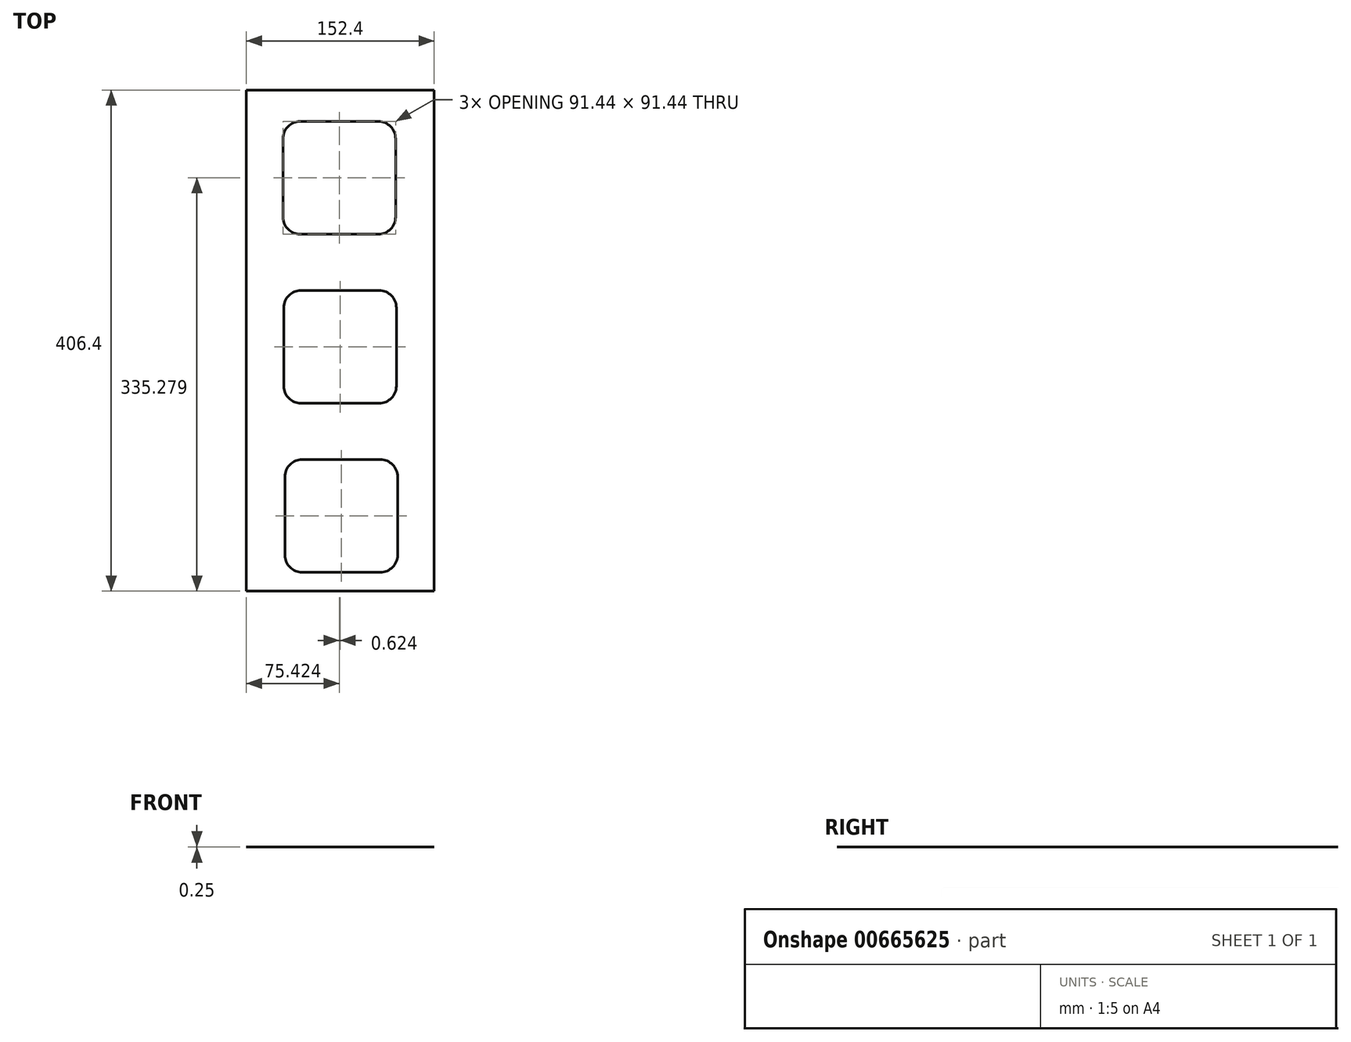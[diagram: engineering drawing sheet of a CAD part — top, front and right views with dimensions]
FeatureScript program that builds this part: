
annotation { "Feature Type Name" : "Feature", "Feature Type Description" : "" }
export const myFeature = defineFeature(function(context is Context, id is Id, definition is map)
    precondition{}
    {
        {
            var Q0;
            Q0=qCreatedBy(makeId("Top.planeOp"),FACE);
            var sketch = newSketch(context, id + "F0", { "sketchPlane" : qUnion([Q0])});
            skLineSegment(sketch, "E0.bottom", {"start": v(-76.2, 289.33) * mm, "end": v(76.2, 289.33) * mm});
            skLineSegment(sketch, "E0.top", {"start": v(-76.2, -117.07) * mm, "end": v(76.2, -117.07) * mm});
            skLineSegment(sketch, "E0.left", {"start": v(-76.2, 289.33) * mm, "end": v(-76.2, -117.07) * mm});
            skLineSegment(sketch, "E0.right", {"start": v(76.2, 289.33) * mm, "end": v(76.2, -117.07) * mm});
            skLineSegment(sketch, "E1", {"start": v(0, 187.73) * mm, "end": v(0, -142.9) * mm, "construction": true});
            skPoint(sketch, "E1.endSnap0", {"position": v(0, -117.07) * mm});
            skSolve(sketch);
        }
        {
            var Q0;
            Q0=qSketchRegion(id+"F0",true);
            extrude(context, id + "F1", {"entities" : qUnion([Q0]), "depth" : 0.25 * mm, "offsetDistance" : 25.4 * mm});
        }
        {
            var Q0;
            Q0=makeQuery(id+"F1.opExtrude","CAP_FACE",FACE,{"disambiguationData":[OSD([sQuery(id+"F0.wireOp",EDGE,"E0.bottom"),sQuery(id+"F0.wireOp",EDGE,"E0.top"),sQuery(id+"F0.wireOp",EDGE,"E0.left"),sQuery(id+"F0.wireOp",EDGE,"E0.right")])],"isStart":false});
            var sketch = newSketch(context, id + "F2", { "sketchPlane" : qUnion([Q0])});
            skLineSegment(sketch, "E2", {"start": v(0, 183.82) * mm, "end": v(0, -138.36) * mm, "construction": true});
            skLineSegment(sketch, "E3.bottom", {"start": v(-32.53, 263.93) * mm, "end": v(30.97, 263.93) * mm});
            skLineSegment(sketch, "E3.top", {"start": v(-32.53, 172.49) * mm, "end": v(30.97, 172.49) * mm});
            skLineSegment(sketch, "E3.left", {"start": v(-46.5, 249.96) * mm, "end": v(-46.5, 186.46) * mm});
            skLineSegment(sketch, "E3.right", {"start": v(44.94, 249.96) * mm, "end": v(44.94, 186.46) * mm});
            skPoint(sketch, "E4.visualSharp", {"position": v(-46.5, 263.93) * mm});
            skArc(sketch, "E4.filletArc", {"start": v(-32.53, 263.93) * mm, "mid": v(-42.4, 259.84) * mm, "end": v(-46.5, 249.96) * mm});
            skPoint(sketch, "E5.visualSharp", {"position": v(44.94, 263.93) * mm});
            skArc(sketch, "E5.filletArc", {"start": v(44.94, 249.96) * mm, "mid": v(40.85, 259.84) * mm, "end": v(30.97, 263.93) * mm});
            skPoint(sketch, "E6.visualSharp", {"position": v(44.94, 172.49) * mm});
            skArc(sketch, "E6.filletArc", {"start": v(30.97, 172.49) * mm, "mid": v(40.85, 176.58) * mm, "end": v(44.94, 186.46) * mm});
            skPoint(sketch, "E7.visualSharp", {"position": v(-46.5, 172.49) * mm});
            skArc(sketch, "E7.filletArc", {"start": v(-46.5, 186.46) * mm, "mid": v(-42.4, 176.58) * mm, "end": v(-32.53, 172.49) * mm});
            skSolve(sketch);
        }
        {
            var Q0;
            Q0=makeQuery(id+"F1.opExtrude","CAP_FACE",FACE,{"disambiguationData":[OSD([sQuery(id+"F0.wireOp",EDGE,"E0.bottom"),sQuery(id+"F0.wireOp",EDGE,"E0.top"),sQuery(id+"F0.wireOp",EDGE,"E0.left"),sQuery(id+"F0.wireOp",EDGE,"E0.right")])],"isStart":false});
            var sketch = newSketch(context, id + "F3", { "sketchPlane" : qUnion([Q0])});
            skLineSegment(sketch, "E8", {"start": v(0, 0) * mm, "end": v(0, -132.12) * mm, "construction": true});
            skLineSegment(sketch, "E9.bottom", {"start": v(-31.9, 126.77) * mm, "end": v(31.6, 126.77) * mm});
            skLineSegment(sketch, "E9.top", {"start": v(-31.9, 35.33) * mm, "end": v(31.6, 35.33) * mm});
            skLineSegment(sketch, "E9.left", {"start": v(-45.87, 112.8) * mm, "end": v(-45.87, 49.3) * mm});
            skLineSegment(sketch, "E9.right", {"start": v(45.57, 112.8) * mm, "end": v(45.57, 49.3) * mm});
            skPoint(sketch, "E10.visualSharp", {"position": v(-45.87, 126.77) * mm});
            skArc(sketch, "E10.filletArc", {"start": v(-31.9, 126.77) * mm, "mid": v(-41.78, 122.68) * mm, "end": v(-45.87, 112.8) * mm});
            skPoint(sketch, "E11.visualSharp", {"position": v(45.57, 126.77) * mm});
            skArc(sketch, "E11.filletArc", {"start": v(45.57, 112.8) * mm, "mid": v(41.48, 122.68) * mm, "end": v(31.6, 126.77) * mm});
            skPoint(sketch, "E12.visualSharp", {"position": v(45.57, 35.33) * mm});
            skArc(sketch, "E12.filletArc", {"start": v(31.6, 35.33) * mm, "mid": v(41.48, 39.42) * mm, "end": v(45.57, 49.3) * mm});
            skPoint(sketch, "E13.visualSharp", {"position": v(-45.87, 35.33) * mm});
            skArc(sketch, "E13.filletArc", {"start": v(-45.87, 49.3) * mm, "mid": v(-41.78, 39.42) * mm, "end": v(-31.9, 35.33) * mm});
            skSolve(sketch);
        }
        {
            var Q0;
            Q0=qSketchRegion(id+"F3",true);
            extrude(context, id + "F4", {"entities" : qUnion([Q0]), "operationType" : NewBodyOperationType.REMOVE, "endBound" : BoundingType.THROUGH_ALL, "oppositeDirection" : true, "depth" : 25.4 * mm, "offsetDistance" : 25.4 * mm});
        }
        {
            var Q0;
            Q0=qSketchRegion(id+"F2",true);
            extrude(context, id + "F5", {"entities" : qUnion([Q0]), "operationType" : NewBodyOperationType.REMOVE, "endBound" : BoundingType.THROUGH_ALL, "oppositeDirection" : true, "depth" : 25.4 * mm, "offsetDistance" : 25.4 * mm});
        }
        {
            var Q0;
            Q0=makeQuery(id+"F2.imprint","IMPRINT",FACE,{"disambiguationData":[TD([[makeQuery(id+"F2.imprint","IMPRINT",EDGE,{"derivedFrom":sQuery(id+"F2.wireOp",EDGE,"E3.bottom")}),1.0]])]});
            var sketch = newSketch(context, id + "F6", { "sketchPlane" : qUnion([Q0])});
            skLineSegment(sketch, "E14.bottom", {"start": v(-30.92, -10.4) * mm, "end": v(32.58, -10.4) * mm});
            skLineSegment(sketch, "E14.top", {"start": v(-30.92, -101.83) * mm, "end": v(32.58, -101.83) * mm});
            skLineSegment(sketch, "E14.left", {"start": v(-44.89, -24.36) * mm, "end": v(-44.89, -87.86) * mm});
            skLineSegment(sketch, "E14.right", {"start": v(46.55, -24.36) * mm, "end": v(46.55, -87.86) * mm});
            skPoint(sketch, "E15.visualSharp", {"position": v(-44.89, -10.4) * mm});
            skArc(sketch, "E15.filletArc", {"start": v(-30.92, -10.4) * mm, "mid": v(-40.8, -14.48) * mm, "end": v(-44.89, -24.36) * mm});
            skPoint(sketch, "E16.visualSharp", {"position": v(46.55, -10.4) * mm});
            skArc(sketch, "E16.filletArc", {"start": v(46.55, -24.36) * mm, "mid": v(42.46, -14.48) * mm, "end": v(32.58, -10.4) * mm});
            skPoint(sketch, "E17.visualSharp", {"position": v(46.55, -101.83) * mm});
            skArc(sketch, "E17.filletArc", {"start": v(32.58, -101.83) * mm, "mid": v(42.46, -97.74) * mm, "end": v(46.55, -87.86) * mm});
            skPoint(sketch, "E18.visualSharp", {"position": v(-44.89, -101.83) * mm});
            skArc(sketch, "E18.filletArc", {"start": v(-44.89, -87.86) * mm, "mid": v(-40.8, -97.74) * mm, "end": v(-30.92, -101.83) * mm});
            skSolve(sketch);
        }
        {
            var Q0;
            Q0=qSketchRegion(id+"F6",true);
            extrude(context, id + "F7", {"entities" : qUnion([Q0]), "operationType" : NewBodyOperationType.REMOVE, "endBound" : BoundingType.THROUGH_ALL, "oppositeDirection" : true, "depth" : 25.4 * mm, "offsetDistance" : 25.4 * mm});
        }
    });
